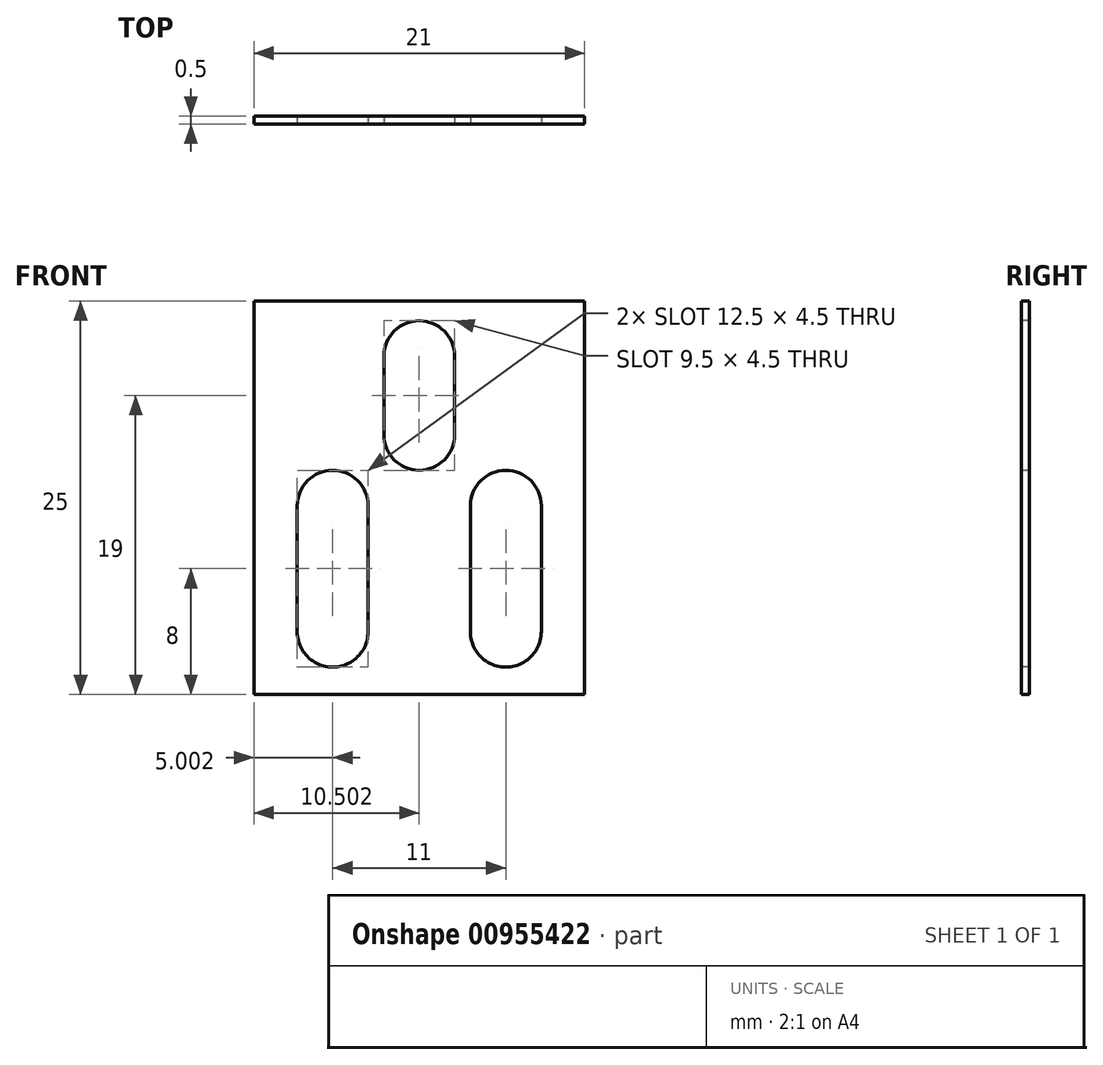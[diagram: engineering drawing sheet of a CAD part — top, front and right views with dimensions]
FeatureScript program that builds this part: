
annotation { "Feature Type Name" : "Feature", "Feature Type Description" : "" }
export const myFeature = defineFeature(function(context is Context, id is Id, definition is map)
    precondition{}
    {
        {
            var Q0;
            Q0=qCreatedBy(makeId("Front.planeOp"),FACE);
            var sketch = newSketch(context, id + "F0", { "sketchPlane" : qUnion([Q0])});
            skLineSegment(sketch, "E0.bottom", {"start": v(-8.1, -10) * mm, "end": v(12.9, -10) * mm});
            skLineSegment(sketch, "E0.top", {"start": v(-8.1, 15) * mm, "end": v(12.9, 15) * mm});
            skLineSegment(sketch, "E0.left", {"start": v(-8.1, -10) * mm, "end": v(-8.1, 15) * mm});
            skLineSegment(sketch, "E0.right", {"start": v(12.9, -10) * mm, "end": v(12.9, 15) * mm});
            skSolve(sketch);
        }
        {
            var Q0;
            Q0 = qSketchRegion(id + "F0", true);
            extrude(context, id + "F1", {"entities" : qUnion([Q0]), "depth" : 0.5 * mm, "offsetDistance" : 25 * mm});
        }
        {
            var Q0;
            Q0=makeQuery(id+"F1.opExtrude","CAP_FACE",FACE,{"disambiguationData":[OSD([sQuery(id+"F0.wireOp",EDGE,"E0.bottom"),sQuery(id+"F0.wireOp",EDGE,"E0.top"),sQuery(id+"F0.wireOp",EDGE,"E0.left"),sQuery(id+"F0.wireOp",EDGE,"E0.right")])],"isStart":false});
            var sketch = newSketch(context, id + "F2", { "sketchPlane" : qUnion([Q0])});
            skLineSegment(sketch, "E1.left", {"start": v(-0.86, -6) * mm, "end": v(-0.86, 2) * mm});
            skLineSegment(sketch, "E1.right", {"start": v(-5.36, -6) * mm, "end": v(-5.36, 2) * mm});
            skPoint(sketch, "E1.middle", {"position": v(-3.1, -2) * mm});
            skArc(sketch, "E2", {"start": v(-0.86, 2) * mm, "mid": v(-3.1, 4.25) * mm, "end": v(-5.36, 2) * mm});
            skArc(sketch, "E3", {"start": v(-5.36, -6) * mm, "mid": v(-3.1, -8.25) * mm, "end": v(-0.86, -6) * mm});
            skLineSegment(sketch, "E4", {"start": v(2.4, 11.57) * mm, "end": v(2.4, -15.97) * mm});
            skLineSegment(sketch, "E5.MirrorCS", {"start": v(5.64, -6) * mm, "end": v(5.64, 2) * mm});
            skArc(sketch, "E6.MirrorCS", {"start": v(5.64, 2) * mm, "mid": v(7.9, 4.25) * mm, "end": v(10.14, 2) * mm});
            skLineSegment(sketch, "E7.MirrorCS", {"start": v(10.14, -6) * mm, "end": v(10.14, 2) * mm});
            skArc(sketch, "E8.MirrorCS", {"start": v(10.14, -6) * mm, "mid": v(7.9, -8.25) * mm, "end": v(5.64, -6) * mm});
            skSolve(sketch);
        }
        {
            var Q0;
            Q0 = qSketchRegion(id + "F2", true);
            extrude(context, id + "F3", {"entities" : qUnion([Q0]), "operationType" : NewBodyOperationType.REMOVE, "oppositeDirection" : true, "depth" : 25 * mm, "offsetDistance" : 25 * mm});
        }
        {
            var Q0;
            Q0=makeQuery(id+"F1.opExtrude","CAP_FACE",FACE,{"disambiguationData":[OSD([sQuery(id+"F0.wireOp",EDGE,"E0.bottom"),sQuery(id+"F0.wireOp",EDGE,"E0.top"),sQuery(id+"F0.wireOp",EDGE,"E0.left"),sQuery(id+"F0.wireOp",EDGE,"E0.right")])],"isStart":false});
            var sketch = newSketch(context, id + "F4", { "sketchPlane" : qUnion([Q0])});
            skLineSegment(sketch, "E9.bottom", {"start": v(4.64, 11.5) * mm, "end": v(0.14, 11.5) * mm});
            skLineSegment(sketch, "E9.top", {"start": v(4.64, 6.5) * mm, "end": v(0.14, 6.5) * mm});
            skLineSegment(sketch, "E9.left", {"start": v(4.64, 11.5) * mm, "end": v(4.64, 6.5) * mm});
            skLineSegment(sketch, "E9.right", {"start": v(0.14, 11.5) * mm, "end": v(0.14, 6.5) * mm});
            skPoint(sketch, "E9.middle", {"position": v(2.4, 9) * mm});
            skArc(sketch, "E10", {"start": v(4.64, 11.5) * mm, "mid": v(2.4, 13.75) * mm, "end": v(0.14, 11.5) * mm});
            skArc(sketch, "E11", {"start": v(0.14, 6.5) * mm, "mid": v(2.4, 4.25) * mm, "end": v(4.64, 6.5) * mm});
            skSolve(sketch);
        }
        {
            var Q0;
            Q0 = qSketchRegion(id + "F4", true);
            extrude(context, id + "F5", {"entities" : qUnion([Q0]), "operationType" : NewBodyOperationType.REMOVE, "oppositeDirection" : true, "depth" : 25 * mm, "offsetDistance" : 25 * mm});
        }
    });
